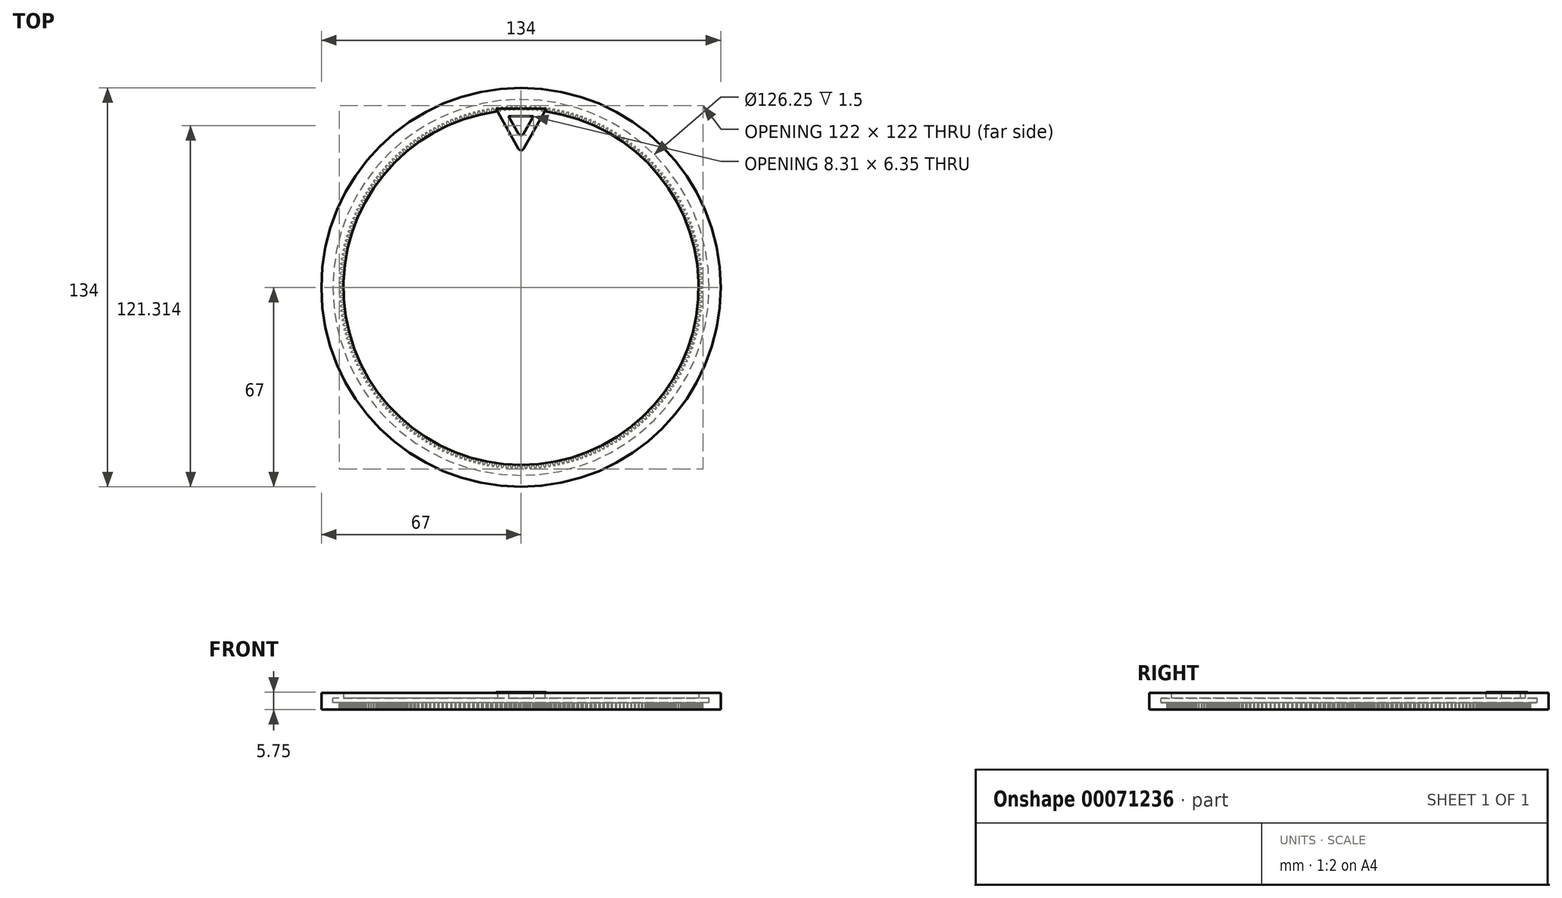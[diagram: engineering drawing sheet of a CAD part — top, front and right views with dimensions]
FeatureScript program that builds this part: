
annotation { "Feature Type Name" : "Feature", "Feature Type Description" : "" }
export const myFeature = defineFeature(function(context is Context, id is Id, definition is map)
    precondition{}
    {
        {
            var Q0;
            Q0=qCreatedBy(makeId("Top.planeOp"),FACE);
            var sketch = newSketch(context, id + "F0", { "sketchPlane" : qUnion([Q0])});
            skCircle(sketch, "E0", {"center": v(0, 0) * mm, "radius": 67 * mm});
            skCircle(sketch, "E1", {"center": v(0, 0) * mm, "radius": 59.6 * mm});
            skSolve(sketch);
        }
        {
            var Q0;
            Q0=makeQuery(id+"F0.imprint","IMPRINT",FACE,{"disambiguationData":[TD([[makeQuery(id+"F0.imprint","IMPRINT",EDGE,{"derivedFrom":sQuery(id+"F0.wireOp",EDGE,"E0")}),1.0]])]});
            extrude(context, id + "F1", {"entities" : qUnion([Q0]), "endBound" : BoundingType.SYMMETRIC, "depth" : 7.5 * mm});
        }
        {
            var Q0;
            Q0=qCreatedBy(makeId("Top.planeOp"),FACE);
            var sketch = newSketch(context, id + "F2", { "sketchPlane" : qUnion([Q0])});
            skCircle(sketch, "E2", {"center": v(0, 0) * mm, "radius": 63.12 * mm});
            skCircle(sketch, "E3", {"center": v(0, 0) * mm, "radius": 63.88 * mm});
            skSolve(sketch);
        }
        {
            var Q0;
            Q0=makeQuery(id+"F2.imprint","IMPRINT",FACE,{"disambiguationData":[TD([[makeQuery(id+"F2.imprint","IMPRINT",EDGE,{"derivedFrom":sQuery(id+"F2.wireOp",EDGE,"E2")}),1.0]])]});
            extrude(context, id + "F3", {"entities" : qUnion([Q0]), "operationType" : NewBodyOperationType.REMOVE, "oppositeDirection" : true, "depth" : 1.5 * mm});
        }
        {
            var Q0;
            Q0=makeQuery(id+"F1.opExtrude","CAP_FACE",FACE,{"disambiguationData":[OSD([sQuery(id+"F0.wireOp",EDGE,"E0"),sQuery(id+"F0.wireOp",EDGE,"E1")])],"isStart":false});
            extrude(context, id + "F4", {"entities" : qUnion([Q0]), "operationType" : NewBodyOperationType.REMOVE, "oppositeDirection" : true, "depth" : 2 * mm});
        }
        {
            var Q0;
            Q0=qCreatedBy(makeId("Top.planeOp"),FACE);
            var sketch = newSketch(context, id + "F5", { "sketchPlane" : qUnion([Q0])});
            skCircle(sketch, "E4", {"center": v(0, 0) * mm, "radius": 61 * mm, "construction": true});
            skLineSegment(sketch, "E5", {"start": v(0, 0) * mm, "end": v(61, 0) * mm, "construction": true});
            skLineSegment(sketch, "E6", {"start": v(61, 0.15) * mm, "end": v(61, -0.15) * mm});
            skPoint(sketch, "E7", {"position": v(59.4, 0) * mm});
            skLineSegment(sketch, "E8", {"start": v(59.4, 0.67) * mm, "end": v(59.4, -0.67) * mm});
            skLineSegment(sketch, "E9", {"start": v(59.4, -0.68) * mm, "end": v(61, -0.15) * mm});
            skLineSegment(sketch, "E10", {"start": v(59.4, 0.68) * mm, "end": v(61, 0.15) * mm});
            skSolve(sketch);
        }
        {
            var Q0;
            Q0=makeQuery(id+"F5.imprint","IMPRINT",FACE,{"disambiguationData":[TD([[makeQuery(id+"F5.imprint","IMPRINT",EDGE,{"derivedFrom":sQuery(id+"F5.wireOp",EDGE,"E6")}),-1.0]])]});
            extrude(context, id + "F6", {"entities" : qUnion([Q0]), "operationType" : NewBodyOperationType.REMOVE, "oppositeDirection" : true, "depth" : 6.5 * mm});
        }
        {
            var Q0;
            Q0=makeQuery(id+"F6.boolean.opBoolean","COPY",FACE,{"derivedFrom":makeQuery(id+"F6.opExtrude","SWEPT_FACE",FACE,{"disambiguationData":[OSD([sQuery(id+"F5.wireOp",EDGE,"E10")])]})});
            var Q1;
            Q1=makeQuery(id+"F6.boolean.opBoolean","COPY",FACE,{"derivedFrom":makeQuery(id+"F6.opExtrude","SWEPT_FACE",FACE,{"disambiguationData":[OSD([sQuery(id+"F5.wireOp",EDGE,"E6")])]})});
            var Q2;
            Q2=makeQuery(id+"F6.boolean.opBoolean","COPY",FACE,{"derivedFrom":makeQuery(id+"F6.opExtrude","SWEPT_FACE",FACE,{"disambiguationData":[OSD([sQuery(id+"F5.wireOp",EDGE,"E9")])]})});
            var Q3;
            {var subQ0=sQuery(id+"F0.wireOp",EDGE,"E1");Q3=makeQuery(id+"F3.boolean.opBoolean","SPLIT",FACE,{"disambiguationData":[TD([makeQuery(id+"F3.opExtrude","CAP_FACE",FACE,{"disambiguationData":[OSD([sQuery(id+"F2.wireOp",EDGE,"E2")])],"isStart":true})])],"derivedFrom":makeQuery(id+"F1.opExtrude","SWEPT_FACE",FACE,{"disambiguationData":[OSD([subQ0])]})});}
            circularPattern(context, id + "F7", {"faces" : qUnion([Q0, Q1, Q2]), "axis" : qUnion([Q3]), "angle" : 360 * degree, "instanceCount" : 240, "equalSpace" : true, "patternType" : PatternType.FACE});
        }
        {
            var Q0;
            Q0=qCreatedBy(makeId("Top.planeOp"),FACE);
            var sketch = newSketch(context, id + "F8", { "sketchPlane" : qUnion([Q0])});
            skLineSegment(sketch, "E11", {"start": v(0, 0) * mm, "end": v(0, 45) * mm, "construction": true});
            skLineSegment(sketch, "E12", {"start": v(0, 0) * mm, "end": v(8.43, 59.99) * mm, "construction": true});
            skLineSegment(sketch, "E13", {"start": v(8.43, 59.99) * mm, "end": v(0, 59.99) * mm});
            skLineSegment(sketch, "E14", {"start": v(0, 45) * mm, "end": v(8.43, 59.99) * mm});
            skLineSegment(sketch, "E15.MirrorCS", {"start": v(-8.43, 59.99) * mm, "end": v(0, 59.99) * mm});
            skLineSegment(sketch, "E16.MirrorCS", {"start": v(0, 45) * mm, "end": v(-8.43, 59.99) * mm});
            skLineSegment(sketch, "E17.0", {"start": v(0, 50.1) * mm, "end": v(4.16, 57.49) * mm});
            skLineSegment(sketch, "E17.1", {"start": v(0, 50.1) * mm, "end": v(-4.16, 57.49) * mm});
            skLineSegment(sketch, "E17.2", {"start": v(-4.16, 57.49) * mm, "end": v(0, 57.49) * mm});
            skLineSegment(sketch, "E17.3", {"start": v(4.16, 57.49) * mm, "end": v(0, 57.49) * mm});
            skSolve(sketch);
        }
        {
            var Q0;
            Q0=makeQuery(id+"F8.imprint","IMPRINT",FACE,{"disambiguationData":[TD([[makeQuery(id+"F8.imprint","IMPRINT",EDGE,{"derivedFrom":sQuery(id+"F8.wireOp",EDGE,"E13")}),1.0]])]});
            extrude(context, id + "F9", {"entities" : qUnion([Q0]), "operationType" : NewBodyOperationType.ADD, "depth" : 2 * mm});
        }
        {
            var Q0;
            Q0=makeQuery(id+"F9.opExtrude","SWEPT_EDGE",EDGE,{"disambiguationData":[OSD([sQuery(id+"F8.wireOp",EDGE,"E14"),sQuery(id+"F8.wireOp",EDGE,"E16.MirrorCS")])]});
            var Q1;
            Q1=makeQuery(id+"F9.opExtrude","SWEPT_EDGE",EDGE,{"disambiguationData":[OSD([sQuery(id+"F8.wireOp",EDGE,"E17.0"),sQuery(id+"F8.wireOp",EDGE,"E17.1")])]});
            fillet(context, id + "F10", {"entities" : qUnion([Q0, Q1]), "radius" : 1 * mm, "tangentPropagation" : true, "allowEdgeOverflow" : false});
        }
    });
